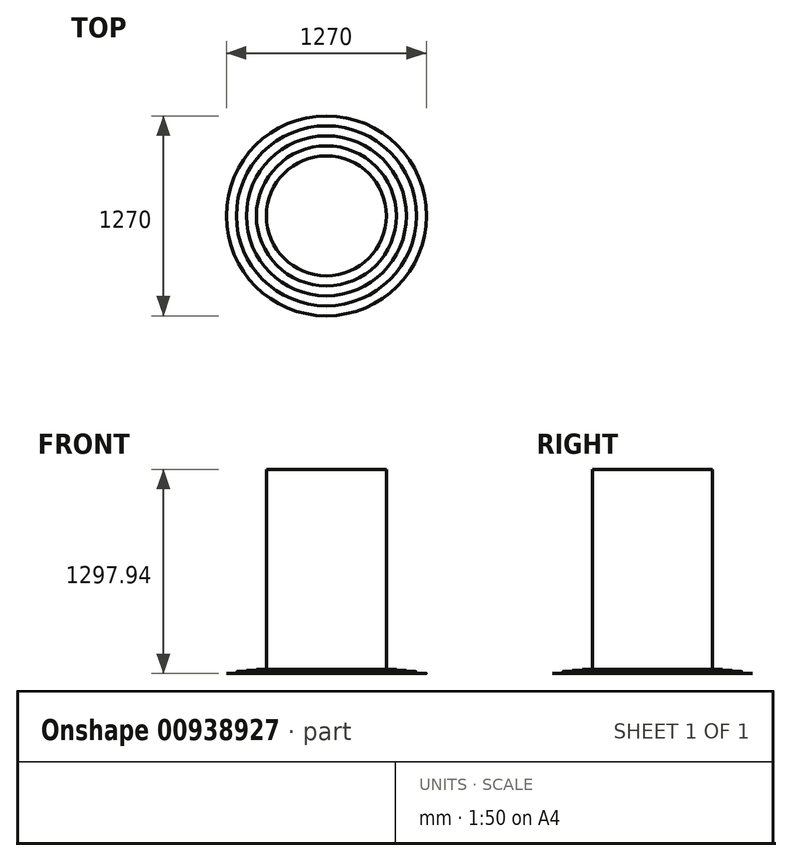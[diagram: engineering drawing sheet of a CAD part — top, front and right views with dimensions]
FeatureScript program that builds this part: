
annotation { "Feature Type Name" : "Feature", "Feature Type Description" : "" }
export const myFeature = defineFeature(function(context is Context, id is Id, definition is map)
    precondition{}
    {
        {
            var Q0;
            Q0=qCreatedBy(makeId("Top.planeOp"),FACE);
            var sketch = newSketch(context, id + "F0", { "sketchPlane" : qUnion([Q0])});
            skCircle(sketch, "E0", {"center": v(0, 0) * mm, "radius": 635 * mm});
            skSolve(sketch);
        }
        {
            var Q0;
            Q0=makeQuery(id+"F0.imprint","IMPRINT",FACE,{"disambiguationData":[TD([[makeQuery(id+"F0.imprint","IMPRINT",EDGE,{"derivedFrom":sQuery(id+"F0.wireOp",EDGE,"E0")}),1.0]])]});
            extrude(context, id + "F1", {"entities" : qUnion([Q0]), "depth" : 2.54 * mm, "offsetDistance" : 25.4 * mm});
        }
        {
            var Q0;
            Q0=makeQuery(id+"F1.opExtrude","CAP_FACE",FACE,{"disambiguationData":[OSD([sQuery(id+"F0.wireOp",EDGE,"E0")])],"isStart":false});
            var sketch = newSketch(context, id + "F2", { "sketchPlane" : qUnion([Q0])});
            skCircle(sketch, "E1", {"center": v(0, 0) * mm, "radius": 571.5 * mm});
            skSolve(sketch);
        }
        {
            var Q0;
            Q0=makeQuery(id+"F2.imprint","IMPRINT",FACE,{"disambiguationData":[TD([[makeQuery(id+"F2.imprint","IMPRINT",EDGE,{"derivedFrom":sQuery(id+"F2.wireOp",EDGE,"E1")}),1.0]])]});
            extrude(context, id + "F3", {"entities" : qUnion([Q0]), "operationType" : NewBodyOperationType.ADD, "depth" : 10.16 * mm, "offsetDistance" : 25.4 * mm});
        }
        {
            var Q0;
            Q0=makeQuery(id+"F3.opExtrude","CAP_FACE",FACE,{"disambiguationData":[OSD([sQuery(id+"F2.wireOp",EDGE,"E1")])],"isStart":false});
            fillet(context, id + "F4", {"entities" : qUnion([Q0]), "radius" : 5.08 * mm, "tangentPropagation" : true, "allowEdgeOverflow" : false});
        }
        {
            var Q0;
            Q0=makeQuery(id+"F3.opExtrude","CAP_FACE",FACE,{"disambiguationData":[OSD([sQuery(id+"F2.wireOp",EDGE,"E1")])],"isStart":false});
            var sketch = newSketch(context, id + "F5", { "sketchPlane" : qUnion([Q0])});
            skCircle(sketch, "E2", {"center": v(0, 0) * mm, "radius": 508 * mm});
            skSolve(sketch);
        }
        {
            var Q0;
            Q0=makeQuery(id+"F5.imprint","IMPRINT",FACE,{"disambiguationData":[TD([[makeQuery(id+"F5.imprint","IMPRINT",EDGE,{"derivedFrom":sQuery(id+"F5.wireOp",EDGE,"E2")}),1.0]])]});
            extrude(context, id + "F6", {"entities" : qUnion([Q0]), "operationType" : NewBodyOperationType.ADD, "depth" : 7.62 * mm, "offsetDistance" : 25.4 * mm});
        }
        {
            var Q0;
            Q0=makeQuery(id+"F6.opExtrude","CAP_EDGE",EDGE,{"disambiguationData":[OSD([sQuery(id+"F5.wireOp",EDGE,"E2")])],"isStart":false});
            fillet(context, id + "F7", {"entities" : qUnion([Q0]), "radius" : 5.08 * mm, "tangentPropagation" : true, "allowEdgeOverflow" : false});
        }
        {
            var Q0;
            Q0=makeQuery(id+"F6.opExtrude","CAP_FACE",FACE,{"disambiguationData":[OSD([sQuery(id+"F5.wireOp",EDGE,"E2")])],"isStart":false});
            var sketch = newSketch(context, id + "F8", { "sketchPlane" : qUnion([Q0])});
            skCircle(sketch, "E3", {"center": v(0, 0) * mm, "radius": 444.5 * mm});
            skSolve(sketch);
        }
        {
            var Q0;
            Q0=makeQuery(id+"F8.imprint","IMPRINT",FACE,{"disambiguationData":[TD([[makeQuery(id+"F8.imprint","IMPRINT",EDGE,{"derivedFrom":sQuery(id+"F8.wireOp",EDGE,"E3")}),1.0]])]});
            extrude(context, id + "F9", {"entities" : qUnion([Q0]), "operationType" : NewBodyOperationType.ADD, "depth" : 7.62 * mm, "offsetDistance" : 25.4 * mm});
        }
        {
            var Q0;
            Q0=makeQuery(id+"F9.opExtrude","CAP_FACE",FACE,{"disambiguationData":[OSD([sQuery(id+"F8.wireOp",EDGE,"E3")])],"isStart":false});
            var sketch = newSketch(context, id + "F10", { "sketchPlane" : qUnion([Q0])});
            skCircle(sketch, "E4", {"center": v(0, 0) * mm, "radius": 381 * mm});
            skSolve(sketch);
        }
        {
            var Q0;
            Q0=makeQuery(id+"F10.imprint","IMPRINT",FACE,{"disambiguationData":[TD([[makeQuery(id+"F10.imprint","IMPRINT",EDGE,{"derivedFrom":sQuery(id+"F10.wireOp",EDGE,"E4")}),1.0]])]});
            extrude(context, id + "F11", {"entities" : qUnion([Q0]), "depth" : 1270 * mm, "offsetDistance" : 25.4 * mm});
        }
    });
